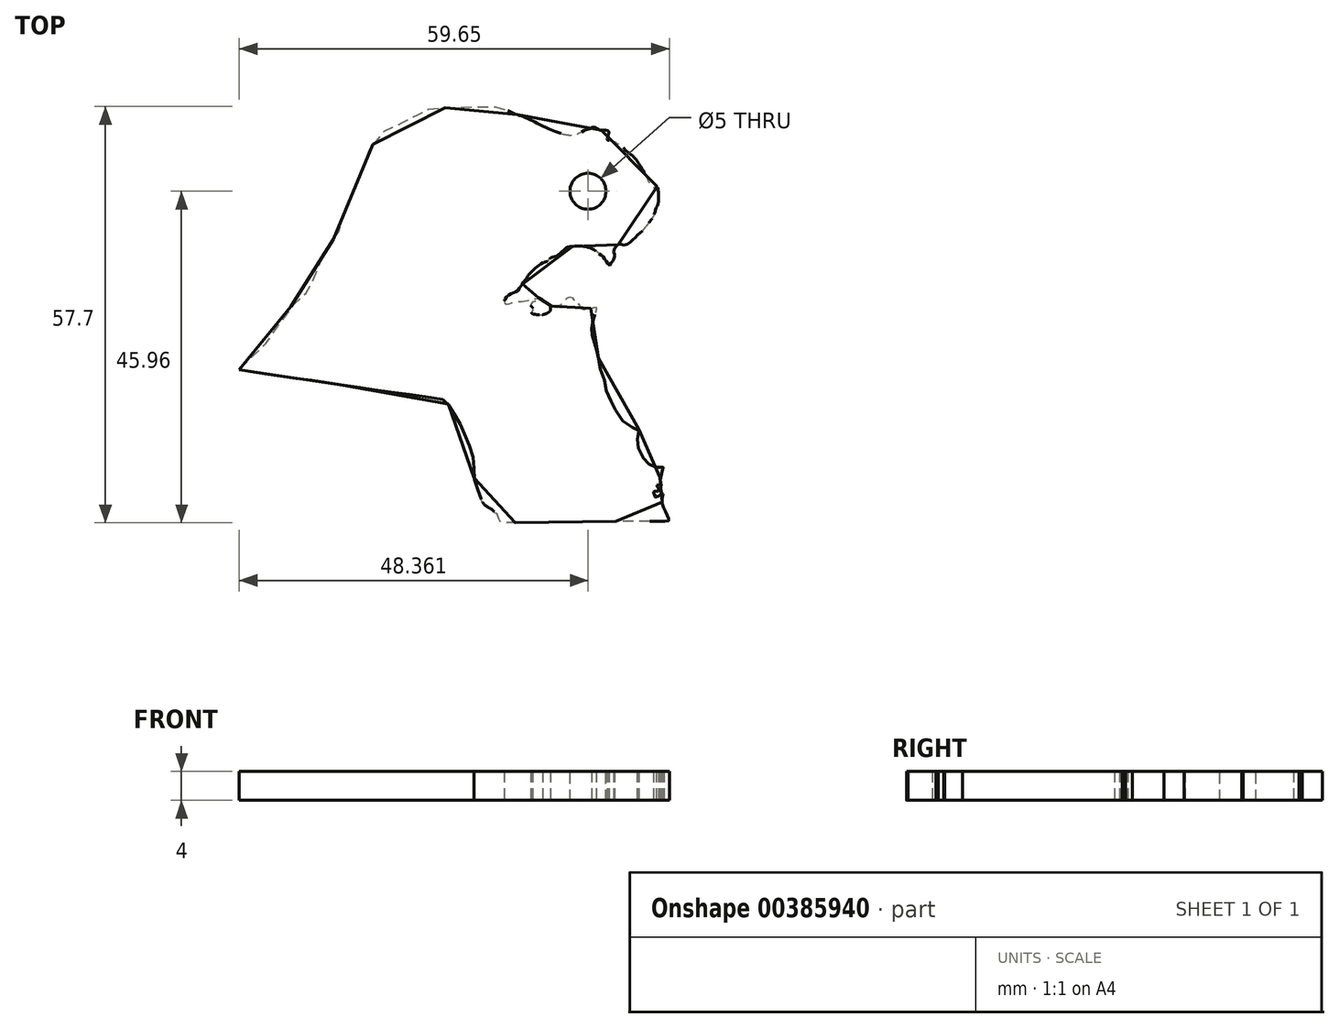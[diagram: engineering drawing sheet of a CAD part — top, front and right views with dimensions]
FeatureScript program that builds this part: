
annotation { "Feature Type Name" : "Feature", "Feature Type Description" : "" }
export const myFeature = defineFeature(function(context is Context, id is Id, definition is map)
    precondition{}
    {
        {
            var Q0;
            Q0=qCreatedBy(makeId("Top.planeOp"),FACE);
            var sketch = newSketch(context, id + "F0", { "sketchPlane" : qUnion([Q0])});
            skLineSegment(sketch, "E0", {"start": v(30.16, 29.1) * mm, "end": v(-29.84, -28.79) * mm, "construction": true});
            skFitSpline(sketch, "E1", {"points": [v(-29.63, -7.44) * mm, v(-29.28, -6.94) * mm, v(-28.76, -6.43) * mm, v(-28.17, -5.89) * mm, v(-27.5, -5.4) * mm, v(-26.73, -4.84) * mm, v(-26.18, -4.34) * mm, v(-25.86, -3.7) * mm, v(-25.47, -2.95) * mm, v(-25.07, -2.3) * mm, v(-24.73, -1.95) * mm, v(-24.37, -1.58) * mm, v(-24.04, -1.2) * mm, v(-23.65, -0.72) * mm, v(-23.36, -0.26) * mm, v(-23.1, 0.26) * mm, v(-22.95, 0.6) * mm, v(-22.7, 0.99) * mm, v(-22.46, 1.3) * mm, v(-22.1, 1.56) * mm, v(-21.7, 1.8) * mm, v(-21.29, 2.14) * mm, v(-20.89, 2.49) * mm, v(-20.47, 3.03) * mm, v(-20.16, 3.41) * mm, v(-19.84, 3.93) * mm, v(-19.53, 4.54) * mm, v(-19.28, 5.18) * mm, v(-18.99, 5.82) * mm, v(-18.84, 6.4) * mm, v(-18.6, 7) * mm, v(-18.28, 7.65) * mm, v(-17.89, 8.27) * mm, v(-17.6, 8.9) * mm, v(-17.29, 9.45) * mm, v(-17, 10.03) * mm, v(-16.58, 10.61) * mm, v(-16.25, 11.05) * mm, v(-15.81, 11.73) * mm, v(-15.53, 12.45) * mm, v(-15.31, 13.38) * mm, v(-15.1, 14.19) * mm, v(-14.94, 14.94) * mm, v(-14.5, 15.87) * mm, v(-14.07, 16.83) * mm, v(-13.6, 17.76) * mm, v(-13.23, 18.7) * mm, v(-12.89, 19.5) * mm, v(-12.47, 20.63) * mm, v(-12.13, 21.62) * mm, v(-11.56, 22.98) * mm, v(-10.72, 24.31) * mm, v(-10.07, 25.1) * mm, v(-9.26, 25.81) * mm, v(-8.43, 26.37) * mm, v(-7.62, 26.62) * mm, v(-6.96, 26.8) * mm, v(-6.28, 26.96) * mm, v(-5.69, 27.3) * mm, v(-5.2, 27.7) * mm, v(-4.57, 28.02) * mm, v(-4.2, 28.1) * mm, v(-4.02, 28.16) * mm, v(-3.83, 28.34) * mm, v(-3.62, 28.56) * mm, v(-3.38, 28.67) * mm, v(-2.76, 28.83) * mm, v(-2.1, 28.9) * mm, v(-1.5, 28.88) * mm, v(-1.02, 28.89) * mm, v(-0.63, 28.9) * mm, v(-0.24, 28.9) * mm, v(0.28, 28.9) * mm, v(0.8, 28.92) * mm, v(1.42, 28.96) * mm, v(2.04, 28.98) * mm, v(2.77, 28.98) * mm, v(4.04, 28.98) * mm, v(4.62, 29) * mm, v(5.22, 29.02) * mm, v(5.52, 29) * mm, v(5.91, 28.97) * mm, v(6.33, 28.94) * mm, v(6.68, 28.88) * mm, v(6.97, 28.75) * mm, v(7.26, 28.63) * mm, v(7.57, 28.49) * mm, v(7.97, 28.28) * mm, v(8.35, 28.1) * mm, v(8.8, 27.94) * mm, v(9.21, 27.8) * mm, v(9.78, 27.64) * mm, v(10.3, 27.37) * mm, v(10.97, 27.1) * mm, v(11.53, 26.79) * mm, v(12.29, 26.42) * mm, v(13.24, 25.96) * mm, v(13.82, 25.7) * mm, v(14.57, 25.44) * mm, v(15.36, 25.19) * mm, v(16.05, 25.08) * mm, v(16.7, 25.03) * mm, v(18.21, 25.69) * mm, v(19.08, 26) * mm, v(19.55, 26.19) * mm, v(20.2, 25.85) * mm, v(20.54, 25.72) * mm, v(21.35, 25.72) * mm, v(21.63, 25.41) * mm, v(21.38, 24.45) * mm, v(22, 24.3) * mm, v(22.87, 23.86) * mm, v(23.5, 23.42) * mm, v(24.21, 22.7) * mm, v(24.9, 22.2) * mm, v(25.67, 21.28) * mm, v(26.17, 20.5) * mm, v(26.73, 19.54) * mm, v(27.16, 18.6) * mm, v(27.42, 18.22) * mm, v(27.63, 17.9) * mm, v(27.91, 17.8) * mm, v(28.08, 17.92) * mm, v(28.16, 18) * mm, v(28.33, 17.9) * mm, v(28.44, 17.62) * mm, v(28.48, 17.27) * mm, v(28.5, 16.79) * mm, v(28.5, 16.26) * mm, v(28.5, 15.79) * mm, v(28.42, 15.45) * mm, v(28.2, 14.98) * mm, v(28.04, 14.47) * mm, v(27.94, 14.13) * mm, v(27.61, 13.5) * mm, v(27.04, 12.71) * mm, v(26.6, 12.19) * mm, v(26.25, 11.72) * mm, v(25.74, 11.3) * mm, v(25.21, 10.8) * mm, v(24.84, 10.43) * mm, v(24.14, 9.94) * mm, v(23.52, 9.83) * mm, v(23, 9.92) * mm, v(22.3, 9) * mm, v(22.42, 8.62) * mm, v(22.42, 8.3) * mm, v(22.34, 7.93) * mm, v(22.18, 7.6) * mm, v(21.92, 7.31) * mm, v(21.69, 7.01) * mm, v(21.48, 7.25) * mm, v(21.22, 7.65) * mm, v(20.94, 8.03) * mm, v(20.7, 8.37) * mm, v(20.35, 8.55) * mm, v(20.1, 8.82) * mm, v(19.84, 8.97) * mm, v(19.57, 9.18) * mm, v(19.2, 9.33) * mm, v(18.75, 9.5) * mm, v(18.34, 9.61) * mm, v(18.05, 9.66) * mm, v(17.47, 9.69) * mm, v(17.04, 9.69) * mm, v(16.6, 9.64) * mm, v(16.06, 9.56) * mm, v(15.64, 9.4) * mm, v(15.13, 8.9) * mm, v(14.7, 8.5) * mm, v(14.37, 8.29) * mm, v(14.03, 8.18) * mm, v(13.76, 8.12) * mm, v(13.45, 7.96) * mm, v(13.22, 7.75) * mm, v(13.14, 7.6) * mm, v(12.83, 7.48) * mm, v(12.46, 7.36) * mm, v(12.15, 7.18) * mm, v(11.82, 6.95) * mm, v(11.5, 6.7) * mm, v(11.2, 6.42) * mm, v(10.9, 6.13) * mm, v(10.71, 5.93) * mm, v(10.53, 5.72) * mm, v(10.35, 5.47) * mm, v(10.18, 5.2) * mm, v(10, 4.93) * mm, v(9.68, 4.47) * mm, v(9.45, 4.13) * mm, v(9.25, 3.89) * mm, v(8.98, 3.52) * mm, v(8.64, 3.27) * mm, v(8.17, 3.1) * mm, v(7.8, 2.94) * mm, v(7.43, 2.6) * mm, v(7.2, 2.25) * mm, v(7.11, 2) * mm, v(7.15, 1.79) * mm, v(7.39, 1.64) * mm, v(7.7, 1.65) * mm, v(7.97, 1.74) * mm, v(8.26, 1.87) * mm, v(8.5, 1.96) * mm, v(8.78, 2.01) * mm, v(9.13, 2) * mm, v(9.6, 2) * mm, v(9.96, 2.05) * mm, v(10.37, 2.1) * mm, v(10.67, 2.19) * mm, v(11.13, 2.3) * mm, v(11.56, 2.42) * mm, v(11.94, 2.5) * mm, v(12.22, 2.53) * mm, v(12.35, 2.49) * mm, v(12.42, 2.37) * mm, v(12.4, 2.19) * mm, v(12.2, 2.06) * mm, v(11.95, 2.02) * mm, v(11.65, 1.99) * mm, v(11.26, 1.98) * mm, v(11.05, 1.9) * mm, v(10.88, 1.71) * mm, v(10.8, 1.52) * mm, v(10.88, 1.34) * mm, v(10.97, 1.22) * mm, v(11.05, 1.1) * mm, v(11.05, 0.84) * mm, v(10.96, 0.55) * mm, v(10.98, 0.3) * mm, v(11.29, 0.24) * mm, v(11.7, 0.15) * mm, v(12.15, 0.15) * mm, v(12.61, 0.2) * mm, v(13, 0.34) * mm, v(13.32, 0.52) * mm, v(13.47, 0.64) * mm, v(13.5, 0.9) * mm, v(13.5, 1.1) * mm, v(13.53, 1.25) * mm, v(13.59, 1.35) * mm, v(13.73, 1.36) * mm, v(13.92, 1.31) * mm, v(14.11, 1.24) * mm, v(14.3, 1.19) * mm, v(14.54, 1.18) * mm, v(14.76, 1.27) * mm, v(14.96, 1.47) * mm, v(15.17, 1.72) * mm, v(15.36, 2) * mm, v(15.57, 2.24) * mm, v(15.77, 2.4) * mm, v(15.96, 2.54) * mm, v(16.18, 2.61) * mm, v(16.37, 2.59) * mm, v(16.58, 2.47) * mm, v(16.75, 2.23) * mm, v(16.83, 2.05) * mm, v(16.88, 1.83) * mm, v(16.95, 1.7) * mm, v(17.18, 1.7) * mm, v(17.36, 1.7) * mm, v(17.47, 1.6) * mm, v(17.57, 1.4) * mm, v(17.62, 1.14) * mm, v(17.71, 1) * mm, v(17.95, 0.92) * mm, v(18.28, 0.88) * mm, v(18.66, 0.9) * mm, v(19, 0.98) * mm, v(19.32, 1.12) * mm, v(19.62, 1.2) * mm, v(19.82, 1.25) * mm, v(19.86, 1.14) * mm, v(19.84, 0.98) * mm, v(19.79, 0.6) * mm, v(19.7, 0.27) * mm, v(19.63, 0.08) * mm, v(19.53, -0.19) * mm, v(19.47, -0.48) * mm, v(19.4, -0.75) * mm, v(19.3, -1.09) * mm, v(19.26, -1.4) * mm, v(19.24, -1.82) * mm, v(19.27, -2.01) * mm, v(19.3, -2.25) * mm, v(19.3, -2.5) * mm, v(19.36, -2.8) * mm, v(19.48, -3.26) * mm, v(19.58, -3.6) * mm, v(19.67, -3.9) * mm, v(19.77, -4.32) * mm, v(19.87, -4.6) * mm, v(19.97, -4.97) * mm, v(20.08, -5.47) * mm, v(20.21, -5.9) * mm, v(20.26, -6.27) * mm, v(20.31, -6.8) * mm, v(20.64, -7.92) * mm, v(20.91, -8.55) * mm, v(21.1, -9.17) * mm, v(21.18, -9.88) * mm, v(21.3, -10.52) * mm, v(21.58, -11.2) * mm, v(21.9, -11.83) * mm, v(22.2, -12.45) * mm, v(22.43, -12.86) * mm, v(23.03, -13.83) * mm, v(23.5, -14.5) * mm, v(24.11, -15.04) * mm, v(24.84, -15.41) * mm, v(25.38, -15.57) * mm, v(25.74, -15.61) * mm, v(25.8, -15.92) * mm, v(25.76, -16.51) * mm, v(25.65, -16.8) * mm, v(25.56, -17.28) * mm, v(25.56, -17.69) * mm, v(25.68, -18.23) * mm, v(25.8, -18.53) * mm, v(26.25, -19.47) * mm, v(26.47, -19.83) * mm, v(26.76, -20.19) * mm, v(27.03, -20.45) * mm, v(27.38, -20.72) * mm, v(27.6, -20.86) * mm, v(27.92, -20.95) * mm, v(28.32, -20.96) * mm, v(28.73, -20.94) * mm, v(29, -20.95) * mm, v(29.2, -21.03) * mm, v(29.26, -21.2) * mm, v(29.16, -21.43) * mm, v(29.02, -21.68) * mm, v(28.91, -21.91) * mm, v(28.8, -22.17) * mm, v(28.73, -22.37) * mm, v(28.74, -22.65) * mm, v(28.72, -22.9) * mm, v(28.82, -23.2) * mm, v(28.9, -23.38) * mm, v(28.87, -23.5) * mm, v(28.62, -23.42) * mm, v(28.38, -23.37) * mm, v(28.24, -23.4) * mm, v(28.28, -23.57) * mm, v(28.44, -23.69) * mm, v(28.55, -23.82) * mm, v(28.57, -24.03) * mm, v(28.5, -24.21) * mm, v(28.3, -24.41) * mm, v(28.1, -24.32) * mm, v(27.9, -24.28) * mm, v(27.83, -24.33) * mm, v(27.84, -24.53) * mm, v(27.9, -24.77) * mm, v(28.01, -25) * mm, v(28.08, -25.13) * mm, v(28.28, -25.09) * mm, v(28.51, -24.98) * mm, v(28.76, -24.8) * mm, v(28.96, -24.68) * mm, v(29.09, -24.6) * mm, v(29.14, -24.74) * mm, v(29.14, -24.92) * mm, v(29.04, -25.1) * mm, v(29.04, -25.54) * mm, v(29.03, -25.96) * mm, v(29.14, -26.43) * mm, v(29.37, -26.92) * mm, v(29.6, -27.38) * mm, v(29.83, -27.92) * mm, v(29.94, -28.14) * mm, v(30.01, -28.4) * mm, v(29.75, -28.45) * mm, v(29.38, -28.47) * mm, v(28.96, -28.51) * mm, v(28.6, -28.46) * mm, v(28.18, -28.49) * mm, v(27.81, -28.46) * mm, v(27.5, -28.46) * mm, v(26.6, -28.5) * mm, v(26.06, -28.49) * mm, v(25.48, -28.49) * mm, v(25.01, -28.48) * mm, v(24.36, -28.48) * mm, v(23.73, -28.48) * mm, v(22.83, -28.48) * mm, v(22.09, -28.5) * mm, v(21.19, -28.48) * mm, v(18.97, -28.53) * mm, v(18.15, -28.56) * mm, v(17.5, -28.56) * mm, v(16.67, -28.56) * mm, v(16, -28.57) * mm, v(14.9, -28.58) * mm, v(14.06, -28.58) * mm, v(13.07, -28.58) * mm, v(11.98, -28.6) * mm, v(10.9, -28.63) * mm, v(10.21, -28.63) * mm, v(9.4, -28.64) * mm, v(8.79, -28.65) * mm, v(7.63, -28.66) * mm, v(6.8, -28.67) * mm, v(6.65, -28.66) * mm, v(6.58, -28.46) * mm, v(6.42, -28.17) * mm, v(6.31, -27.86) * mm, v(6.2, -27.6) * mm, v(6.02, -27.37) * mm, v(5.9, -27.22) * mm, v(5.67, -27.1) * mm, v(5.46, -26.93) * mm, v(5.15, -26.7) * mm, v(4.89, -26.53) * mm, v(4.48, -26.25) * mm, v(4.2, -25.93) * mm, v(4, -25.64) * mm, v(3.83, -25.18) * mm, v(3.64, -24.68) * mm, v(3.47, -24.18) * mm, v(3.28, -23.7) * mm, v(3.1, -23.2) * mm, v(2.98, -22.78) * mm, v(2.93, -22.3) * mm, v(2.95, -21.61) * mm, v(2.93, -21) * mm, v(2.93, -20.5) * mm, v(2.91, -20.01) * mm, v(2.78, -19.42) * mm, v(2.6, -18.83) * mm, v(2.34, -18.08) * mm, v(2.07, -17.45) * mm, v(1.72, -16.63) * mm, v(1.47, -16.14) * mm, v(1.35, -15.83) * mm, v(1.16, -15.36) * mm, v(0.95, -14.78) * mm, v(0.63, -14.13) * mm, v(0.21, -13.69) * mm, v(-0.16, -13.2) * mm, v(-0.39, -12.8) * mm, v(-0.58, -12.38) * mm, v(-0.77, -11.99) * mm, v(-0.93, -11.75) * mm, v(-1.27, -11.62) * mm, v(-1.83, -11.53) * mm, v(-3.53, -11.28) * mm, v(-4.82, -11.1) * mm, v(-5.99, -10.93) * mm, v(-7.49, -10.72) * mm, v(-8.98, -10.5) * mm, v(-10.33, -10.3) * mm, v(-11.15, -10.2) * mm, v(-12, -10.05) * mm, v(-13.3, -9.87) * mm, v(-14.42, -9.71) * mm, v(-15.74, -9.53) * mm, v(-17.29, -9.3) * mm, v(-18.18, -9.16) * mm, v(-19.2, -9) * mm, v(-20.49, -8.82) * mm, v(-21.62, -8.67) * mm, v(-22.86, -8.5) * mm, v(-23.8, -8.34) * mm, v(-24.63, -8.21) * mm, v(-25.98, -8.02) * mm, v(-27.12, -7.87) * mm, v(-27.93, -7.75) * mm, v(-28.6, -7.65) * mm, v(-29.4, -7.55) * mm, v(-29.63, -7.44) * mm]});
            skSolve(sketch);
        }
        {
            var Q0;
            Q0=makeQuery(id+"F0.imprint","IMPRINT",FACE,{"disambiguationData":[TD([[makeQuery(id+"F0.imprint","IMPRINT",EDGE,{"derivedFrom":sQuery(id+"F0.wireOp",EDGE,"E1")}),-1.0]])]});
            extrude(context, id + "F1", {"entities" : qUnion([Q0]), "depth" : 4 * mm});
        }
        {
            var Q0;
            Q0=makeQuery(id+"F1.opExtrude","CAP_FACE",FACE,{"disambiguationData":[OSD([sQuery(id+"F0.wireOp",EDGE,"E1")])],"isStart":false});
            var sketch = newSketch(context, id + "F2", { "sketchPlane" : qUnion([Q0])});
            skCircle(sketch, "E2", {"center": v(18.73, 17.28) * mm, "radius": 2.5 * mm});
            skSolve(sketch);
        }
        {
            var Q0;
            Q0=makeQuery(id+"F2.imprint","IMPRINT",FACE,{"disambiguationData":[TD([[makeQuery(id+"F2.imprint","IMPRINT",EDGE,{"derivedFrom":sQuery(id+"F2.wireOp",EDGE,"E2")}),1.0]])]});
            extrude(context, id + "F3", {"entities" : qUnion([Q0]), "operationType" : NewBodyOperationType.REMOVE, "oppositeDirection" : true, "depth" : 25 * mm});
        }
    });
